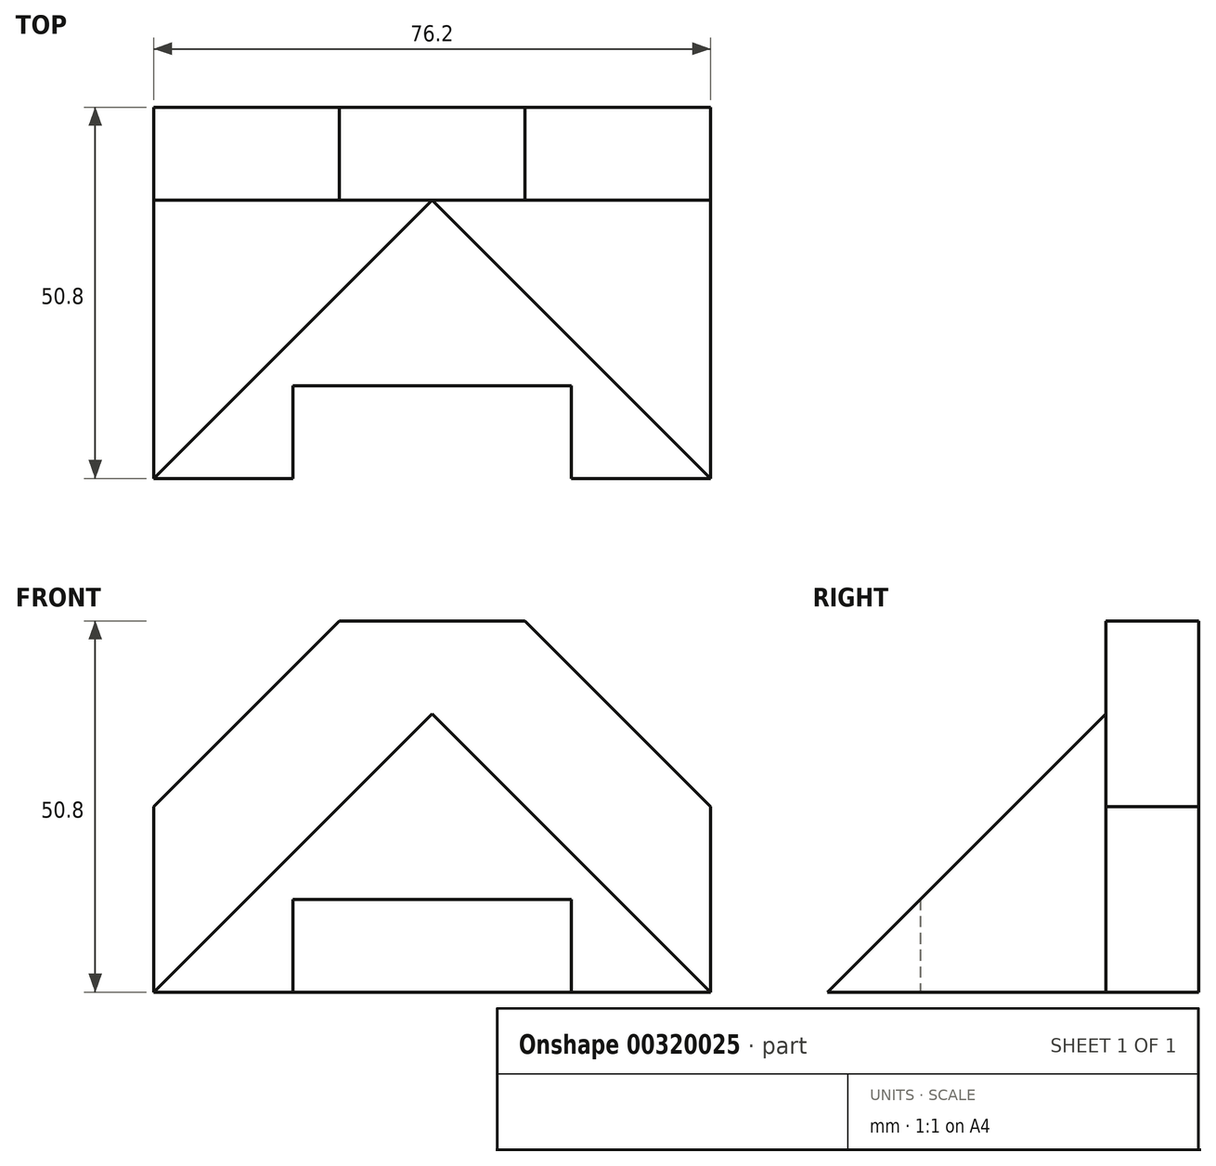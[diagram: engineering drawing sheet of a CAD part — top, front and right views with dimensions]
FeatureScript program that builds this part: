
annotation { "Feature Type Name" : "Feature", "Feature Type Description" : "" }
export const myFeature = defineFeature(function(context is Context, id is Id, definition is map)
    precondition{}
    {
        {
            var Q0;
            Q0=qCreatedBy(makeId("Right.planeOp"),FACE);
            var sketch = newSketch(context, id + "F0", { "sketchPlane" : qUnion([Q0])});
            skLineSegment(sketch, "E0", {"start": v(0, 0) * mm, "end": v(50.8, 0) * mm});
            skLineSegment(sketch, "E1", {"start": v(50.8, 0) * mm, "end": v(50.8, 50.8) * mm});
            skLineSegment(sketch, "E2", {"start": v(50.8, 50.8) * mm, "end": v(38.1, 50.8) * mm});
            skLineSegment(sketch, "E3", {"start": v(38.1, 50.8) * mm, "end": v(38.1, 0) * mm});
            skLineSegment(sketch, "E4", {"start": v(38.1, 38.1) * mm, "end": v(0, 0) * mm});
            skLineSegment(sketch, "E5", {"start": v(38.1, 25.4) * mm, "end": v(50.8, 25.4) * mm});
            skLineSegment(sketch, "E6", {"start": v(12.7, 12.7) * mm, "end": v(12.7, 0) * mm});
            skSolve(sketch);
        }
        {
            var Q0;
            {var subQ3=sQuery(id+"F0.wireOp",EDGE,"E6");Q0=makeQuery(id+"F0.imprint","IMPRINT",FACE,{"disambiguationData":[TD([[makeQuery(id+"F0.imprint","IMPRINT",EDGE,{"derivedFrom":subQ3}),-1.0]])]});}
            var Q1;
            {var subQ5=sQuery(id+"F0.wireOp",EDGE,"E5");Q1=makeQuery(id+"F0.imprint","IMPRINT",FACE,{"disambiguationData":[TD([[makeQuery(id+"F0.imprint","IMPRINT",EDGE,{"derivedFrom":subQ5}),-1.0]])]});}
            var Q2;
            {var subQ3=sQuery(id+"F0.wireOp",EDGE,"E6");Q2=makeQuery(id+"F0.imprint","IMPRINT",FACE,{"disambiguationData":[TD([[makeQuery(id+"F0.imprint","IMPRINT",EDGE,{"derivedFrom":subQ3}),1.0]])]});}
            extrude(context, id + "F1", {"entities" : qUnion([Q0, Q1, Q2]), "endBound" : BoundingType.SYMMETRIC, "depth" : 76.2 * mm});
        }
        {
            var Q0;
            Q0 = qSketchRegion(id + "F0", true);
            extrude(context, id + "F2", {"entities" : qUnion([Q0]), "operationType" : NewBodyOperationType.ADD, "endBound" : BoundingType.SYMMETRIC, "depth" : 25.4 * mm});
        }
        {
            var Q0;
            {var subQ3=sQuery(id+"F0.wireOp",EDGE,"E6");Q0=makeQuery(id+"F0.imprint","IMPRINT",FACE,{"disambiguationData":[TD([[makeQuery(id+"F0.imprint","IMPRINT",EDGE,{"derivedFrom":subQ3}),-1.0]])]});}
            extrude(context, id + "F3", {"entities" : qUnion([Q0]), "operationType" : NewBodyOperationType.REMOVE, "endBound" : BoundingType.SYMMETRIC, "oppositeDirection" : true, "depth" : 38.1 * mm});
        }
        {
            var Q0;
            Q0=qCreatedBy(makeId("Front.planeOp"),FACE);
            var sketch = newSketch(context, id + "F4", { "sketchPlane" : qUnion([Q0])});
            skLineSegment(sketch, "E7", {"start": v(-38.1, 0) * mm, "end": v(38.1, 0) * mm});
            skLineSegment(sketch, "E8", {"start": v(38.1, 0) * mm, "end": v(0, 38.1) * mm});
            skLineSegment(sketch, "E9", {"start": v(0, 38.1) * mm, "end": v(-38.1, 0) * mm});
            skLineSegment(sketch, "E10.top", {"start": v(-38.1, 38.1) * mm, "end": v(38.1, 38.1) * mm});
            skLineSegment(sketch, "E10.left", {"start": v(-38.1, 0) * mm, "end": v(-38.1, 38.1) * mm});
            skLineSegment(sketch, "E10.right", {"start": v(38.1, 0) * mm, "end": v(38.1, 38.1) * mm});
            skSolve(sketch);
        }
        {
            var Q0;
            {var subQ0=sQuery(id+"F4.wireOp",EDGE,"E8");Q0=makeQuery(id+"F4.imprint","IMPRINT",FACE,{"disambiguationData":[TD([[makeQuery(id+"F4.imprint","IMPRINT",EDGE,{"derivedFrom":subQ0}),-1.0]])]});}
            var Q1;
            {var subQ0=sQuery(id+"F4.wireOp",EDGE,"E9");Q1=makeQuery(id+"F4.imprint","IMPRINT",FACE,{"disambiguationData":[TD([[makeQuery(id+"F4.imprint","IMPRINT",EDGE,{"derivedFrom":subQ0}),-1.0]])]});}
            var Q2;
            {var subQ0=sQuery(id+"F0.wireOp",EDGE,"E4");var subQ1=sQuery(id+"F0.wireOp",EDGE,"E3");var subQ2=sQuery(id+"F0.wireOp",EDGE,"E1");var subQ3=sQuery(id+"F0.wireOp",EDGE,"E0");var subQ4=sQuery(id+"F0.wireOp",EDGE,"E5");Q2=makeQuery(id+"F2.boolean.opBoolean","SPLIT",FACE,{"disambiguationData":[TD([makeQuery(id+"F1.opExtrude","CAP_FACE",FACE,{"disambiguationData":[OSD([subQ3,subQ2,subQ1,subQ0,subQ4])],"isStart":false})])],"derivedFrom":makeQuery(id+"F1.opExtrude","SWEPT_FACE",FACE,{"disambiguationData":[OSD([subQ1])]})});}
            extrude(context, id + "F5", {"entities" : qUnion([Q0, Q1]), "operationType" : NewBodyOperationType.REMOVE, "endBound" : BoundingType.UP_TO_SURFACE, "oppositeDirection" : true, "endBoundEntityFace" : qUnion([Q2]), "depth" : 25.4 * mm});
        }
        {
            var Q0;
            {var subQ0=sQuery(id+"F0.wireOp",EDGE,"E1");Q0=makeQuery(id+"F2.boolean.opBoolean","MERGE",FACE,{"derivedFrom":[makeQuery(id+"F1.opExtrude","SWEPT_FACE",FACE,{"disambiguationData":[OSD([subQ0])]}),makeQuery(id+"F2.opExtrude","SWEPT_FACE",FACE,{"disambiguationData":[OSD([subQ0])]})]});}
            var sketch = newSketch(context, id + "F6", { "sketchPlane" : qUnion([Q0])});
            skLineSegment(sketch, "E11", {"start": v(12.7, 50.8) * mm, "end": v(38.1, 25.4) * mm});
            skLineSegment(sketch, "E12", {"start": v(38.1, 25.4) * mm, "end": v(12.7, 25.4) * mm});
            skLineSegment(sketch, "E13", {"start": v(12.7, 25.4) * mm, "end": v(12.7, 50.8) * mm});
            skLineSegment(sketch, "E14", {"start": v(-12.7, 50.8) * mm, "end": v(-12.7, 25.4) * mm});
            skLineSegment(sketch, "E15", {"start": v(-12.7, 25.4) * mm, "end": v(-38.1, 25.4) * mm});
            skLineSegment(sketch, "E16", {"start": v(-38.1, 25.4) * mm, "end": v(-12.7, 50.8) * mm});
            skSolve(sketch);
        }
        {
            var Q0;
            Q0=makeQuery(id+"F6.imprint","IMPRINT",FACE,{"disambiguationData":[TD([[makeQuery(id+"F6.imprint","IMPRINT",EDGE,{"derivedFrom":sQuery(id+"F6.wireOp",EDGE,"E14")}),1.0]])]});
            var Q1;
            Q1=makeQuery(id+"F6.imprint","IMPRINT",FACE,{"disambiguationData":[TD([[makeQuery(id+"F6.imprint","IMPRINT",EDGE,{"derivedFrom":sQuery(id+"F6.wireOp",EDGE,"E11")}),-1.0]])]});
            var Q2;
            Q2=makeQuery(id+"F5.boolean.opBoolean","COPY",FACE,{"derivedFrom":makeQuery(id+"F5.opExtrude","CAP_FACE",FACE,{"disambiguationData":[OSD([sQuery(id+"F4.wireOp",EDGE,"E9"),sQuery(id+"F4.wireOp",EDGE,"E10.top"),sQuery(id+"F4.wireOp",EDGE,"E10.left")])],"isStart":false})});
            extrude(context, id + "F7", {"entities" : qUnion([Q0, Q1]), "operationType" : NewBodyOperationType.ADD, "endBound" : BoundingType.UP_TO_SURFACE, "oppositeDirection" : true, "endBoundEntityFace" : qUnion([Q2]), "depth" : 25.4 * mm});
        }
    });
